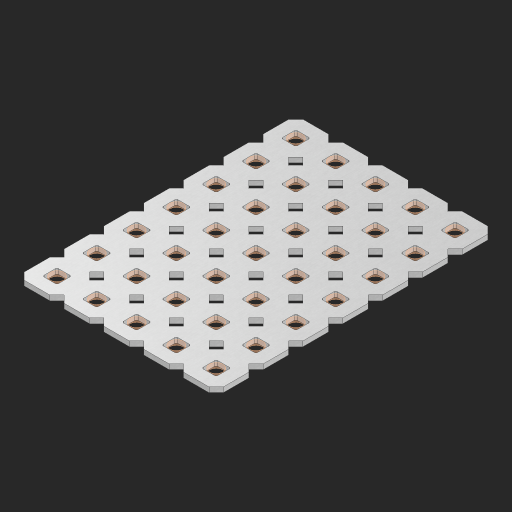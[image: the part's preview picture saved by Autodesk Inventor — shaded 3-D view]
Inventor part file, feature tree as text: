
AUTODESK INVENTOR PART (.ipt)
format: ipt  version: 2023 (Build 270158000, 158)  size: 703,488 bytes
history: native  units: in
note: dims shown in document units (in); Inventor stores cm internally (conversion verified against a paired STEP export)
features: other x36, extrude x34, sketch x2, pattern_linear x1
ambient origin geometry x8: Origin, YZ Plane, XZ Plane, XY Plane, X Axis, Y Axis, Z Axis, Center Point
bodies: Solid1 (feature_tree), Body (feature_tree)
feature tree (73):
  pattern_linear  "Rectangular Pattern1"  Spacing1=0.09in  [1 undecoded]
  sketch  "Sketch1"  dims[d1=0.5in]
  sketch  "Sketch2"  dims[d2=0.182in d3=0.09in d4=0.09in d5=0.09in d6=0.09in d7=0.09in d8=0.09in d9=0.09in d10=0.09in d11=0.02in d13=0.0in d14=0.172in d15=0.0625in d16=0.0in d19=0.5in d22=0.5in]
  other  "Srf1"
  other  "Srf126"
  other  "Srf127"
  other  "Srf128"
  other  "Srf129"
  other  "Srf130"
  other  "Srf131"
  other  "Srf268"
  other  "Srf269"
  other  "Srf270"
  other  "Srf271"
  other  "Srf272"
  other  "Srf273"
  other  "Srf274"
  other  "Srf293"
  other  "Srf294"
  other  "Srf295"
  other  "Srf296"
  other  "Srf297"
  other  "Srf298"
  other  "Srf299"
  other  "Srf318"
  other  "Srf319"
  other  "Srf320"
  other  "Srf321"
  other  "Srf322"
  other  "Srf323"
  other  "Srf324"
  other  "Srf343"
  other  "Srf344"
  other  "Srf345"
  other  "Srf346"
  other  "Srf347"
  other  "Srf348"
  other  "Srf349"
  other  "Circle"
  extrude  "ExtrusionSrf126"  Depth=0.09in
  extrude  "ExtrusionSrf127"  Depth=0.09in
  extrude  "ExtrusionSrf128"  Depth=0.09in
  extrude  "ExtrusionSrf129"  Depth=0.09in
  extrude  "ExtrusionSrf130"  Depth=0.09in
  extrude  "ExtrusionSrf131"  Depth=0.09in
  extrude  "ExtrusionSrf268"  Depth=0.09in
  extrude  "ExtrusionSrf269"  Depth=0.02in
  extrude  "ExtrusionSrf270"  TaperAngle=0.0deg  [1 undecoded]
  extrude  "ExtrusionSrf271"  Depth=0.5in
  extrude  "ExtrusionSrf272"  Depth=0.0625in TaperAngle=0.0deg
  extrude  "ExtrusionSrf273"  Depth=0.5in
  extrude  "ExtrusionSrf274"  Depth=0.5in
  extrude  "ExtrusionSrf293"  [1 undecoded]
  extrude  "ExtrusionSrf294"  [1 undecoded]
  extrude  "ExtrusionSrf295"  [1 undecoded]
  extrude  "ExtrusionSrf296"  [1 undecoded]
  extrude  "ExtrusionSrf297"  [1 undecoded]
  extrude  "ExtrusionSrf298"  [1 undecoded]
  extrude  "ExtrusionSrf299"  [1 undecoded]
  extrude  "ExtrusionSrf318"  [1 undecoded]
  extrude  "ExtrusionSrf319"  [1 undecoded]
  extrude  "ExtrusionSrf320"  [1 undecoded]
  extrude  "ExtrusionSrf321"  [1 undecoded]
  extrude  "ExtrusionSrf322"  [1 undecoded]
  extrude  "ExtrusionSrf323"  [1 undecoded]
  extrude  "ExtrusionSrf324"  [1 undecoded]
  extrude  "ExtrusionSrf343"  [1 undecoded]
  extrude  "ExtrusionSrf344"  [1 undecoded]
  extrude  "ExtrusionSrf345"  [1 undecoded]
  extrude  "ExtrusionSrf346"  [1 undecoded]
  extrude  "ExtrusionSrf347"  [1 undecoded]
  extrude  "ExtrusionSrf348"  [1 undecoded]
  extrude  "ExtrusionSrf349"  [1 undecoded]
note: 23 required parameter values undecoded (feature->parameter linkage not recoverable at this tier; creation-order binding heuristic only, values carry confidence <= 0.55)
